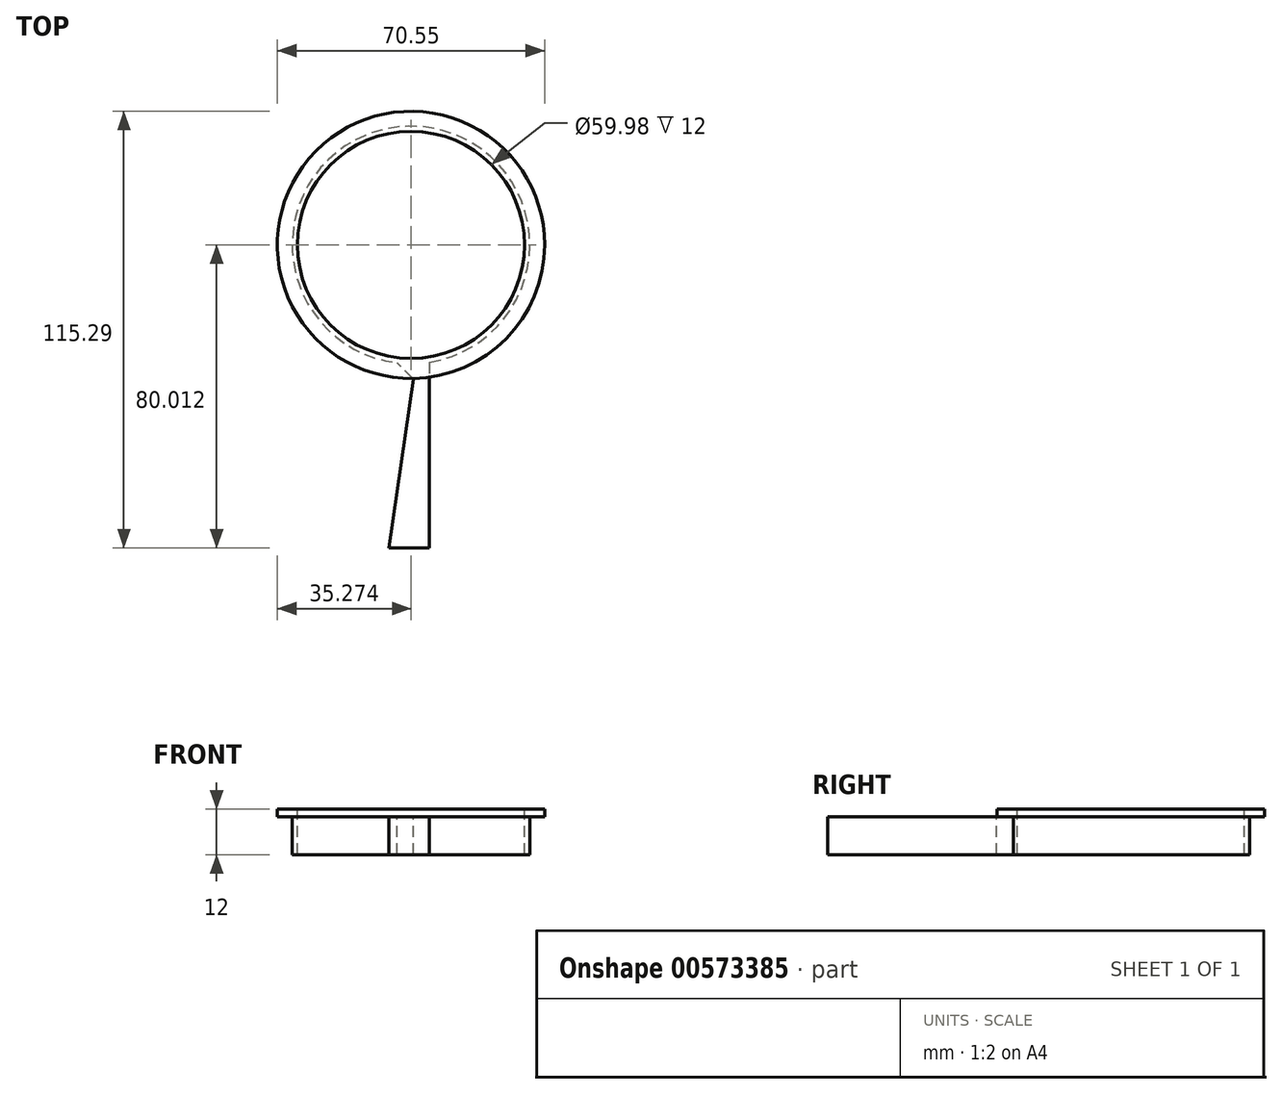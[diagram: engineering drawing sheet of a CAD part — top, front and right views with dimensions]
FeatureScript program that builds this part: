
annotation { "Feature Type Name" : "Feature", "Feature Type Description" : "" }
export const myFeature = defineFeature(function(context is Context, id is Id, definition is map)
    precondition{}
    {
        {
            var Q0;
            Q0=qCreatedBy(makeId("Top.planeOp"),FACE);
            var sketch = newSketch(context, id + "F0", { "sketchPlane" : qUnion([Q0])});
            skLineSegment(sketch, "E0", {"start": v(-10.08, 0) * mm, "end": v(0, 0) * mm});
            skLineSegment(sketch, "E1", {"start": v(0, 0) * mm, "end": v(0, -50.39) * mm});
            skLineSegment(sketch, "E2", {"start": v(0, -50.39) * mm, "end": v(-10.69, -50.39) * mm});
            skLineSegment(sketch, "E3", {"start": v(-10.69, -50.39) * mm, "end": v(-4.28, -5.8) * mm});
            skLineSegment(sketch, "E4", {"start": v(-4.28, -5.8) * mm, "end": v(-10.08, 0) * mm});
            skSolve(sketch);
        }
        {
            var Q0;
            Q0=makeQuery(id+"F0.imprint","IMPRINT",FACE,{"disambiguationData":[TD([[makeQuery(id+"F0.imprint","IMPRINT",EDGE,{"derivedFrom":sQuery(id+"F0.wireOp",EDGE,"E0")}),-1.0]])]});
            extrude(context, id + "F1", {"entities" : qUnion([Q0]), "oppositeDirection" : true, "depth" : 10 * mm, "offsetDistance" : 25 * mm});
        }
        {
            var Q0;
            Q0=qCreatedBy(makeId("Top.planeOp"),FACE);
            var sketch = newSketch(context, id + "F2", { "sketchPlane" : qUnion([Q0])});
            skCircle(sketch, "E5", {"center": v(-4.89, 29.62) * mm, "radius": 31.35 * mm});
            skSolve(sketch);
        }
        {
            var Q0;
            Q0=makeQuery(id+"F2.imprint","IMPRINT",FACE,{"disambiguationData":[TD([[makeQuery(id+"F2.imprint","IMPRINT",EDGE,{"derivedFrom":sQuery(id+"F2.wireOp",EDGE,"E5")}),1.0]])]});
            extrude(context, id + "F3", {"entities" : qUnion([Q0]), "operationType" : NewBodyOperationType.ADD, "oppositeDirection" : true, "depth" : 10 * mm, "offsetDistance" : 25 * mm});
        }
        {
            var Q0;
            Q0=makeQuery(id+"F3.boolean.opBoolean","MERGE",FACE,{"derivedFrom":[makeQuery(id+"F1.opExtrude","CAP_FACE",FACE,{"disambiguationData":[OSD([sQuery(id+"F0.wireOp",EDGE,"E0"),sQuery(id+"F0.wireOp",EDGE,"E1"),sQuery(id+"F0.wireOp",EDGE,"E2"),sQuery(id+"F0.wireOp",EDGE,"E3"),sQuery(id+"F0.wireOp",EDGE,"E4")])],"isStart":true}),makeQuery(id+"F3.opExtrude","CAP_FACE",FACE,{"disambiguationData":[OSD([sQuery(id+"F2.wireOp",EDGE,"E5")])],"isStart":true})]});
            var sketch = newSketch(context, id + "F4", { "sketchPlane" : qUnion([Q0])});
            skCircle(sketch, "E6", {"center": v(-4.89, 29.62) * mm, "radius": 35.28 * mm});
            skSolve(sketch);
        }
        {
            var Q0;
            Q0 = qSketchRegion(id + "F4", true);
            extrude(context, id + "F5", {"entities" : qUnion([Q0]), "operationType" : NewBodyOperationType.ADD, "depth" : 2 * mm, "offsetDistance" : 25 * mm});
        }
        {
            var Q0;
            Q0=makeQuery(id+"F5.opExtrude","CAP_FACE",FACE,{"disambiguationData":[OSD([sQuery(id+"F4.wireOp",EDGE,"E6")])],"isStart":false});
            var sketch = newSketch(context, id + "F6", { "sketchPlane" : qUnion([Q0])});
            skCircle(sketch, "E7", {"center": v(-4.89, 29.62) * mm, "radius": 29.99 * mm});
            skSolve(sketch);
        }
        {
            var Q0;
            Q0=makeQuery(id+"F6.imprint","IMPRINT",FACE,{"disambiguationData":[TD([[makeQuery(id+"F6.imprint","IMPRINT",EDGE,{"derivedFrom":sQuery(id+"F6.wireOp",EDGE,"E7")}),1.0]])]});
            extrude(context, id + "F7", {"entities" : qUnion([Q0]), "operationType" : NewBodyOperationType.REMOVE, "oppositeDirection" : true, "depth" : 25 * mm, "offsetDistance" : 25 * mm});
        }
    });
